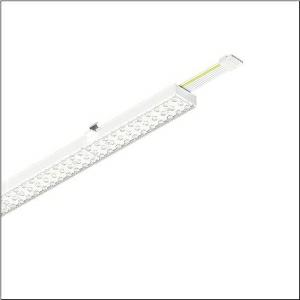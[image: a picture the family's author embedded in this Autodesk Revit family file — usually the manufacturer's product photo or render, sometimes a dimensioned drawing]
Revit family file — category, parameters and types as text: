
# Revit family: trunking_flex_31_51re12dc49b007
name_source: partatom
category: Lighting Fixtures
units: mm (PartAtom-declared; Revit-internal decimal feet)

## family parameters
Cut with Voids When Loaded = No
Host = Face
Light Source = No
Part Type = Normal
Room Calculation Point = No
Round Connector Dimension = Use Diameter
Shared = No

## types (1)
- Trunking Flex 31 (1 x LED, 8900 lm, 53 W, 4000K)
    Apparent Load = 53 VA
    CIE Flux Codes = 65 91 98 99 100
    Color Rendering = 80
    Color Temperature = 4000K
    Default Elevation = 1800 mm
    Description = Trunking Flex 31, luminaire insert, of extruded aluminium section, coated, traffic white (RAL 9016), length: 1.438mm, width: 91mm, height: 53mm, LED rated luminous flux: 8.900lm, light colour: 840, control gear: DALI 2, with system connector: socket, through-wiring: 7x 2.5mm², mains connection: 220..240V, AC, 50/60Hz, rated input power: 53W, primary light control with lens, of plastic, primary optical cover: cover, of PMMA, light emission: direct distribution, protection rating (complete): IP20, insulation class (complete): insulation class I (protective earthing), certification: CE, UKCA, impact resistance: IK02, permissible ambient temperature for indoor applications: -20..+40°C, packaging unit: 1 piece
    Height = 58 mm
    Lamp = 1 x LED
    Lamp Light Flux = 8900 lm
    Lamp Power = 53 W
    Lamp count = 1
    Length = 1438 mm
    Luminous efficacy = 168 lm/W
    Manufacturer = Siteco
    ModVariant = No
    Model = 51RE12DC49B007
    Mounting Place = Ceiling
    Mounting Type = Pendant
    Number of Poles = 1
    OnlyDefault = Yes
    Power Factor = 1
    Product Name = Trunking Flex 31
    Product group = luminaire insert | ceiling pendant
    ProductGroupID = 902
    Protection Class = Protection class I
    Protection Degree = IP 20
    RLX_Detail_Level = 1
    RLX_Emergency_Light_Flux = 0 lm
    RLX_Emergency_Type = 0
    RLX_Emergency_Type_DB = No
    RlxData = <blob elided: 22229 chars, md5=c9b5c09b>
    Socket = socket
    Standby Power = 0 W
    System Light Flux = 8900 lm
    System Power = 53 W
    Type Comments = Product without accessories
    Type Image = l_1297860.jpg
    URL = http://relux.com
    VarID = ---
    Voltage = 0 V
    Weight = 0.00 kg
    Width = 65 mm

## geometry (parser evidence)
native form markers: Blend x4, Sweep x14
no freeform markers — native parametric forms only
